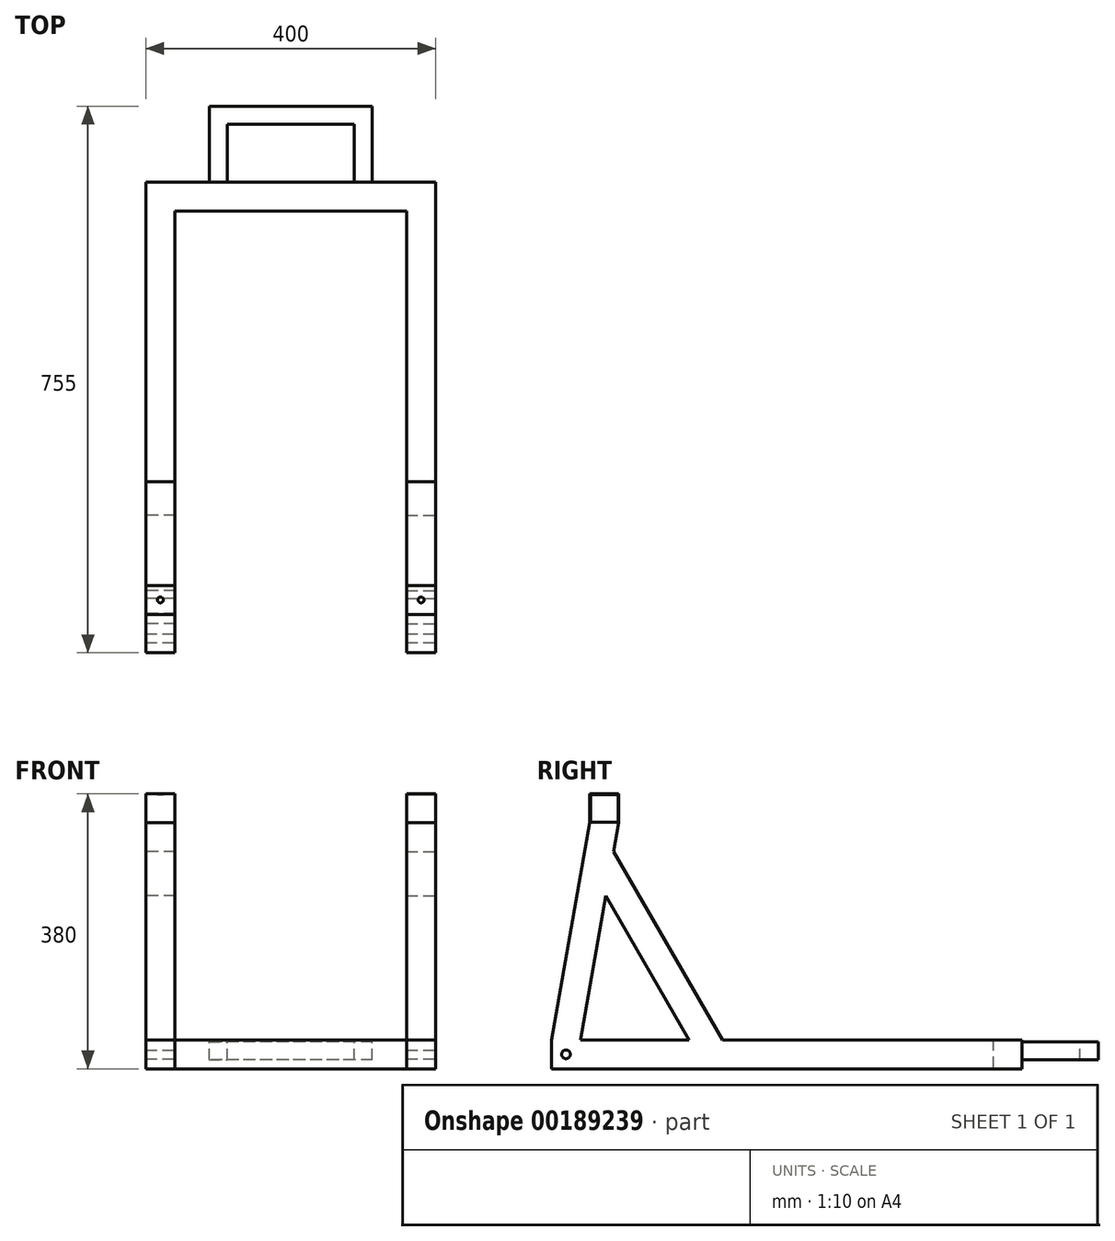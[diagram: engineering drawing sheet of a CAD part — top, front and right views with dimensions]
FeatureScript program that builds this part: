
annotation { "Feature Type Name" : "Feature", "Feature Type Description" : "" }
export const myFeature = defineFeature(function(context is Context, id is Id, definition is map)
    precondition{}
    {
        {
            var Q0;
            Q0=qCreatedBy(makeId("Top.planeOp"),FACE);
            var sketch = newSketch(context, id + "F0", { "sketchPlane" : qUnion([Q0])});
            skLineSegment(sketch, "E0", {"start": v(0, 0) * mm, "end": v(0, 650) * mm});
            skLineSegment(sketch, "E1", {"start": v(0, 650) * mm, "end": v(400, 650) * mm});
            skLineSegment(sketch, "E2", {"start": v(400, 650) * mm, "end": v(400, 0) * mm});
            skLineSegment(sketch, "E3", {"start": v(400, 0) * mm, "end": v(360, 0) * mm});
            skLineSegment(sketch, "E4", {"start": v(360, 0) * mm, "end": v(360, 610) * mm});
            skLineSegment(sketch, "E5", {"start": v(360, 610) * mm, "end": v(40, 610) * mm});
            skLineSegment(sketch, "E6", {"start": v(40, 610) * mm, "end": v(40, 0) * mm});
            skLineSegment(sketch, "E7", {"start": v(40, 0) * mm, "end": v(0, 0) * mm});
            skSolve(sketch);
        }
        {
            var Q0;
            Q0 = qSketchRegion(id + "F0", true);
            extrude(context, id + "F1", {"entities" : qUnion([Q0]), "depth" : 40 * mm});
        }
        {
            var Q0;
            Q0=makeQuery(id+"F1.opExtrude","SWEPT_FACE",FACE,{"disambiguationData":[OSD([sQuery(id+"F0.wireOp",EDGE,"E1")])]});
            var sketch = newSketch(context, id + "F2", { "sketchPlane" : qUnion([Q0])});
            skLineSegment(sketch, "E8", {"start": v(-200, 0) * mm, "end": v(-200, 25) * mm, "construction": true});
            skLineSegment(sketch, "E9", {"start": v(-200, 25) * mm, "end": v(-100, 25) * mm, "construction": true});
            skLineSegment(sketch, "E10.bottom", {"start": v(-87.5, 12.5) * mm, "end": v(-112.5, 12.5) * mm});
            skLineSegment(sketch, "E10.top", {"start": v(-87.5, 37.5) * mm, "end": v(-112.5, 37.5) * mm});
            skLineSegment(sketch, "E10.left", {"start": v(-87.5, 12.5) * mm, "end": v(-87.5, 37.5) * mm});
            skLineSegment(sketch, "E10.right", {"start": v(-112.5, 12.5) * mm, "end": v(-112.5, 37.5) * mm});
            skPoint(sketch, "E10.middle", {"position": v(-100, 25) * mm});
            skLineSegment(sketch, "E11", {"start": v(-200, 25) * mm, "end": v(-300, 25) * mm, "construction": true});
            skLineSegment(sketch, "E12.bottom", {"start": v(-312.5, 12.5) * mm, "end": v(-287.5, 12.5) * mm});
            skLineSegment(sketch, "E12.top", {"start": v(-312.5, 37.5) * mm, "end": v(-287.5, 37.5) * mm});
            skLineSegment(sketch, "E12.left", {"start": v(-312.5, 12.5) * mm, "end": v(-312.5, 37.5) * mm});
            skLineSegment(sketch, "E12.right", {"start": v(-287.5, 12.5) * mm, "end": v(-287.5, 37.5) * mm});
            skPoint(sketch, "E12.middle", {"position": v(-300, 25) * mm});
            skSolve(sketch);
        }
        {
            var Q0;
            Q0 = qSketchRegion(id + "F2", true);
            extrude(context, id + "F3", {"entities" : qUnion([Q0]), "operationType" : NewBodyOperationType.ADD, "depth" : 80 * mm});
        }
        {
            var Q0;
            Q0=makeQuery(id+"F3.opExtrude","CAP_FACE",FACE,{"disambiguationData":[OSD([sQuery(id+"F2.wireOp",EDGE,"E12.bottom"),sQuery(id+"F2.wireOp",EDGE,"E12.top"),sQuery(id+"F2.wireOp",EDGE,"E12.left"),sQuery(id+"F2.wireOp",EDGE,"E12.right")])],"isStart":false});
            var sketch = newSketch(context, id + "F4", { "sketchPlane" : qUnion([Q0])});
            skLineSegment(sketch, "E13.bottom", {"start": v(-312.5, 12.5) * mm, "end": v(-87.5, 12.5) * mm});
            skLineSegment(sketch, "E13.top", {"start": v(-312.5, 37.5) * mm, "end": v(-87.5, 37.5) * mm});
            skLineSegment(sketch, "E13.left", {"start": v(-312.5, 12.5) * mm, "end": v(-312.5, 37.5) * mm});
            skLineSegment(sketch, "E13.right", {"start": v(-87.5, 12.5) * mm, "end": v(-87.5, 37.5) * mm});
            skSolve(sketch);
        }
        {
            var Q0;
            Q0 = qSketchRegion(id + "F4", true);
            extrude(context, id + "F5", {"entities" : qUnion([Q0]), "operationType" : NewBodyOperationType.ADD, "depth" : 25 * mm});
        }
        {
            var Q0;
            Q0=makeQuery(id+"F1.opExtrude","SWEPT_FACE",FACE,{"disambiguationData":[OSD([sQuery(id+"F0.wireOp",EDGE,"E0")])]});
            var sketch = newSketch(context, id + "F6", { "sketchPlane" : qUnion([Q0])});
            skLineSegment(sketch, "E14", {"start": v(0, 40) * mm, "end": v(-52.9, 340) * mm});
            skLineSegment(sketch, "E15", {"start": v(-52.9, 340) * mm, "end": v(-92.9, 340) * mm});
            skLineSegment(sketch, "E16", {"start": v(-92.9, 340) * mm, "end": v(-40, 40) * mm});
            skLineSegment(sketch, "E17", {"start": v(-40, 40) * mm, "end": v(0, 40) * mm});
            skSolve(sketch);
        }
        {
            var Q0;
            Q0 = qSketchRegion(id + "F6", true);
            extrude(context, id + "F7", {"entities" : qUnion([Q0]), "operationType" : NewBodyOperationType.ADD, "oppositeDirection" : true, "depth" : 40 * mm});
        }
        {
            var Q0;
            Q0=makeQuery(id+"F1.opExtrude","SWEPT_FACE",FACE,{"disambiguationData":[OSD([sQuery(id+"F0.wireOp",EDGE,"E2")])]});
            var sketch = newSketch(context, id + "F8", { "sketchPlane" : qUnion([Q0])});
            skLineSegment(sketch, "E18", {"start": v(0, 40) * mm, "end": v(52.9, 340) * mm});
            skLineSegment(sketch, "E19", {"start": v(52.9, 340) * mm, "end": v(92.9, 340) * mm});
            skLineSegment(sketch, "E20", {"start": v(92.9, 340) * mm, "end": v(40, 40) * mm});
            skLineSegment(sketch, "E21", {"start": v(40, 40) * mm, "end": v(0, 40) * mm});
            skSolve(sketch);
        }
        {
            var Q0;
            Q0 = qSketchRegion(id + "F8", true);
            extrude(context, id + "F9", {"entities" : qUnion([Q0]), "operationType" : NewBodyOperationType.ADD, "oppositeDirection" : true, "depth" : 40 * mm});
        }
        {
            var Q0;
            Q0=makeQuery(id+"F9.boolean.opBoolean","MERGE",FACE,{"derivedFrom":[makeQuery(id+"F1.opExtrude","SWEPT_FACE",FACE,{"disambiguationData":[OSD([sQuery(id+"F0.wireOp",EDGE,"E2")])]}),makeQuery(id+"F9.opExtrude","CAP_FACE",FACE,{"disambiguationData":[OSD([sQuery(id+"F8.wireOp",EDGE,"E18"),sQuery(id+"F8.wireOp",EDGE,"E19"),sQuery(id+"F8.wireOp",EDGE,"E20"),sQuery(id+"F8.wireOp",EDGE,"E21")])],"isStart":true})]});
            var sketch = newSketch(context, id + "F10", { "sketchPlane" : qUnion([Q0])});
            skCircle(sketch, "E22", {"center": v(20, 20) * mm, "radius": 6 * mm});
            skSolve(sketch);
        }
        {
            var Q0;
            Q0 = qSketchRegion(id + "F10", true);
            extrude(context, id + "F11", {"entities" : qUnion([Q0]), "operationType" : NewBodyOperationType.REMOVE, "endBound" : BoundingType.THROUGH_ALL, "oppositeDirection" : true, "depth" : 25 * mm});
        }
        {
            var Q0;
            Q0=makeQuery(id+"F9.boolean.opBoolean","MERGE",FACE,{"derivedFrom":[makeQuery(id+"F1.opExtrude","SWEPT_FACE",FACE,{"disambiguationData":[OSD([sQuery(id+"F0.wireOp",EDGE,"E2")])]}),makeQuery(id+"F9.opExtrude","CAP_FACE",FACE,{"disambiguationData":[OSD([sQuery(id+"F8.wireOp",EDGE,"E18"),sQuery(id+"F8.wireOp",EDGE,"E19"),sQuery(id+"F8.wireOp",EDGE,"E20"),sQuery(id+"F8.wireOp",EDGE,"E21")])],"isStart":true})]});
            var sketch = newSketch(context, id + "F12", { "sketchPlane" : qUnion([Q0])});
            skLineSegment(sketch, "E23.bottom", {"start": v(52.9, 340) * mm, "end": v(92.9, 340) * mm});
            skLineSegment(sketch, "E23.top", {"start": v(52.9, 380) * mm, "end": v(92.9, 380) * mm});
            skLineSegment(sketch, "E23.left", {"start": v(52.9, 340) * mm, "end": v(52.9, 380) * mm});
            skLineSegment(sketch, "E23.right", {"start": v(92.9, 340) * mm, "end": v(92.9, 380) * mm});
            skLineSegment(sketch, "E24.bottom", {"start": v(53.9, 341) * mm, "end": v(91.9, 341) * mm});
            skLineSegment(sketch, "E24.top", {"start": v(53.9, 379) * mm, "end": v(91.9, 379) * mm});
            skLineSegment(sketch, "E24.left", {"start": v(53.9, 341) * mm, "end": v(53.9, 379) * mm});
            skLineSegment(sketch, "E24.right", {"start": v(91.9, 341) * mm, "end": v(91.9, 379) * mm});
            skSolve(sketch);
        }
        {
            var Q0;
            Q0=makeQuery(id+"F12.imprint","IMPRINT",FACE,{"disambiguationData":[TD([[makeQuery(id+"F12.imprint","IMPRINT",EDGE,{"derivedFrom":sQuery(id+"F12.wireOp",EDGE,"E23.bottom")}),1.0]])]});
            extrude(context, id + "F13", {"entities" : qUnion([Q0]), "operationType" : NewBodyOperationType.ADD, "oppositeDirection" : true, "depth" : 40 * mm});
        }
        {
            var Q0;
            Q0=makeQuery(id+"F7.boolean.opBoolean","MERGE",FACE,{"derivedFrom":[makeQuery(id+"F1.opExtrude","SWEPT_FACE",FACE,{"disambiguationData":[OSD([sQuery(id+"F0.wireOp",EDGE,"E0")])]}),makeQuery(id+"F7.opExtrude","CAP_FACE",FACE,{"disambiguationData":[OSD([sQuery(id+"F6.wireOp",EDGE,"E14"),sQuery(id+"F6.wireOp",EDGE,"E15"),sQuery(id+"F6.wireOp",EDGE,"E16"),sQuery(id+"F6.wireOp",EDGE,"E17")])],"isStart":true})]});
            var sketch = newSketch(context, id + "F14", { "sketchPlane" : qUnion([Q0])});
            skLineSegment(sketch, "E25.bottom", {"start": v(-92.9, 340) * mm, "end": v(-52.9, 340) * mm});
            skLineSegment(sketch, "E25.top", {"start": v(-92.9, 380) * mm, "end": v(-52.9, 380) * mm});
            skLineSegment(sketch, "E25.left", {"start": v(-92.9, 340) * mm, "end": v(-92.9, 380) * mm});
            skLineSegment(sketch, "E25.right", {"start": v(-52.9, 340) * mm, "end": v(-52.9, 380) * mm});
            skLineSegment(sketch, "E26.bottom", {"start": v(-91.9, 341) * mm, "end": v(-53.9, 341) * mm});
            skLineSegment(sketch, "E26.top", {"start": v(-91.9, 379) * mm, "end": v(-53.9, 379) * mm});
            skLineSegment(sketch, "E26.left", {"start": v(-91.9, 341) * mm, "end": v(-91.9, 379) * mm});
            skLineSegment(sketch, "E26.right", {"start": v(-53.9, 341) * mm, "end": v(-53.9, 379) * mm});
            skSolve(sketch);
        }
        {
            var Q0;
            Q0 = qSketchRegion(id + "F14", true);
            extrude(context, id + "F15", {"entities" : qUnion([Q0]), "operationType" : NewBodyOperationType.ADD, "oppositeDirection" : true, "depth" : 40 * mm});
        }
        {
            var Q0;
            Q0=makeQuery(id+"F15.opExtrude","SWEPT_FACE",FACE,{"disambiguationData":[OSD([sQuery(id+"F14.wireOp",EDGE,"E25.top")])]});
            var sketch = newSketch(context, id + "F16", { "sketchPlane" : qUnion([Q0])});
            skCircle(sketch, "E27", {"center": v(20, 72.9) * mm, "radius": 4 * mm});
            skSolve(sketch);
        }
        {
            var Q0;
            Q0 = qSketchRegion(id + "F16", true);
            extrude(context, id + "F17", {"entities" : qUnion([Q0]), "operationType" : NewBodyOperationType.REMOVE, "oppositeDirection" : true, "depth" : 25 * mm});
        }
        {
            var Q0;
            Q0=makeQuery(id+"F13.opExtrude","SWEPT_FACE",FACE,{"disambiguationData":[OSD([sQuery(id+"F12.wireOp",EDGE,"E23.top")])]});
            var sketch = newSketch(context, id + "F18", { "sketchPlane" : qUnion([Q0])});
            skCircle(sketch, "E28", {"center": v(380, 72.9) * mm, "radius": 4 * mm});
            skSolve(sketch);
        }
        {
            var Q0;
            Q0 = qSketchRegion(id + "F18", true);
            extrude(context, id + "F19", {"entities" : qUnion([Q0]), "operationType" : NewBodyOperationType.REMOVE, "oppositeDirection" : true, "depth" : 25 * mm});
        }
        {
            var Q0;
            Q0=makeQuery(id+"F13.boolean.opBoolean","MERGE",FACE,{"derivedFrom":[makeQuery(id+"F9.boolean.opBoolean","MERGE",FACE,{"derivedFrom":[makeQuery(id+"F1.opExtrude","SWEPT_FACE",FACE,{"disambiguationData":[OSD([sQuery(id+"F0.wireOp",EDGE,"E2")])]}),makeQuery(id+"F9.opExtrude","CAP_FACE",FACE,{"disambiguationData":[OSD([sQuery(id+"F8.wireOp",EDGE,"E18"),sQuery(id+"F8.wireOp",EDGE,"E19"),sQuery(id+"F8.wireOp",EDGE,"E20"),sQuery(id+"F8.wireOp",EDGE,"E21")])],"isStart":true})]}),makeQuery(id+"F13.opExtrude","CAP_FACE",FACE,{"disambiguationData":[OSD([sQuery(id+"F12.wireOp",EDGE,"E23.bottom"),sQuery(id+"F12.wireOp",EDGE,"E23.top"),sQuery(id+"F12.wireOp",EDGE,"E23.left"),sQuery(id+"F12.wireOp",EDGE,"E23.right"),sQuery(id+"F12.wireOp",EDGE,"E24.bottom"),sQuery(id+"F12.wireOp",EDGE,"E24.top"),sQuery(id+"F12.wireOp",EDGE,"E24.left"),sQuery(id+"F12.wireOp",EDGE,"E24.right")])],"isStart":true})]});
            var sketch = newSketch(context, id + "F20", { "sketchPlane" : qUnion([Q0])});
            skLineSegment(sketch, "E29", {"start": v(190, 40) * mm, "end": v(75.1, 239.02) * mm});
            skLineSegment(sketch, "E30", {"start": v(75.1, 239.02) * mm, "end": v(85.9, 300.3) * mm});
            skLineSegment(sketch, "E31", {"start": v(85.9, 300.3) * mm, "end": v(236.19, 40) * mm});
            skLineSegment(sketch, "E32", {"start": v(236.19, 40) * mm, "end": v(190, 40) * mm});
            skSolve(sketch);
        }
        {
            var Q0;
            Q0 = qSketchRegion(id + "F20", true);
            extrude(context, id + "F21", {"entities" : qUnion([Q0]), "operationType" : NewBodyOperationType.ADD, "oppositeDirection" : true, "depth" : 40 * mm});
        }
        {
            var Q0;
            Q0=makeQuery(id+"F15.boolean.opBoolean","MERGE",FACE,{"derivedFrom":[makeQuery(id+"F7.boolean.opBoolean","MERGE",FACE,{"derivedFrom":[makeQuery(id+"F1.opExtrude","SWEPT_FACE",FACE,{"disambiguationData":[OSD([sQuery(id+"F0.wireOp",EDGE,"E0")])]}),makeQuery(id+"F7.opExtrude","CAP_FACE",FACE,{"disambiguationData":[OSD([sQuery(id+"F6.wireOp",EDGE,"E14"),sQuery(id+"F6.wireOp",EDGE,"E15"),sQuery(id+"F6.wireOp",EDGE,"E16"),sQuery(id+"F6.wireOp",EDGE,"E17")])],"isStart":true})]}),makeQuery(id+"F15.opExtrude","CAP_FACE",FACE,{"disambiguationData":[OSD([sQuery(id+"F14.wireOp",EDGE,"E25.bottom"),sQuery(id+"F14.wireOp",EDGE,"E25.top"),sQuery(id+"F14.wireOp",EDGE,"E25.left"),sQuery(id+"F14.wireOp",EDGE,"E25.right"),sQuery(id+"F14.wireOp",EDGE,"E26.bottom"),sQuery(id+"F14.wireOp",EDGE,"E26.top"),sQuery(id+"F14.wireOp",EDGE,"E26.left"),sQuery(id+"F14.wireOp",EDGE,"E26.right")])],"isStart":true})]});
            var sketch = newSketch(context, id + "F22", { "sketchPlane" : qUnion([Q0])});
            skLineSegment(sketch, "E33", {"start": v(-190, 40) * mm, "end": v(-75.1, 239.02) * mm});
            skLineSegment(sketch, "E34", {"start": v(-75.1, 239.02) * mm, "end": v(-85.9, 300.3) * mm});
            skLineSegment(sketch, "E35", {"start": v(-85.9, 300.3) * mm, "end": v(-236.19, 40) * mm});
            skLineSegment(sketch, "E36", {"start": v(-236.19, 40) * mm, "end": v(-190, 40) * mm});
            skSolve(sketch);
        }
        {
            var Q0;
            Q0 = qSketchRegion(id + "F22", true);
            extrude(context, id + "F23", {"entities" : qUnion([Q0]), "operationType" : NewBodyOperationType.ADD, "oppositeDirection" : true, "depth" : 40 * mm});
        }
    });
